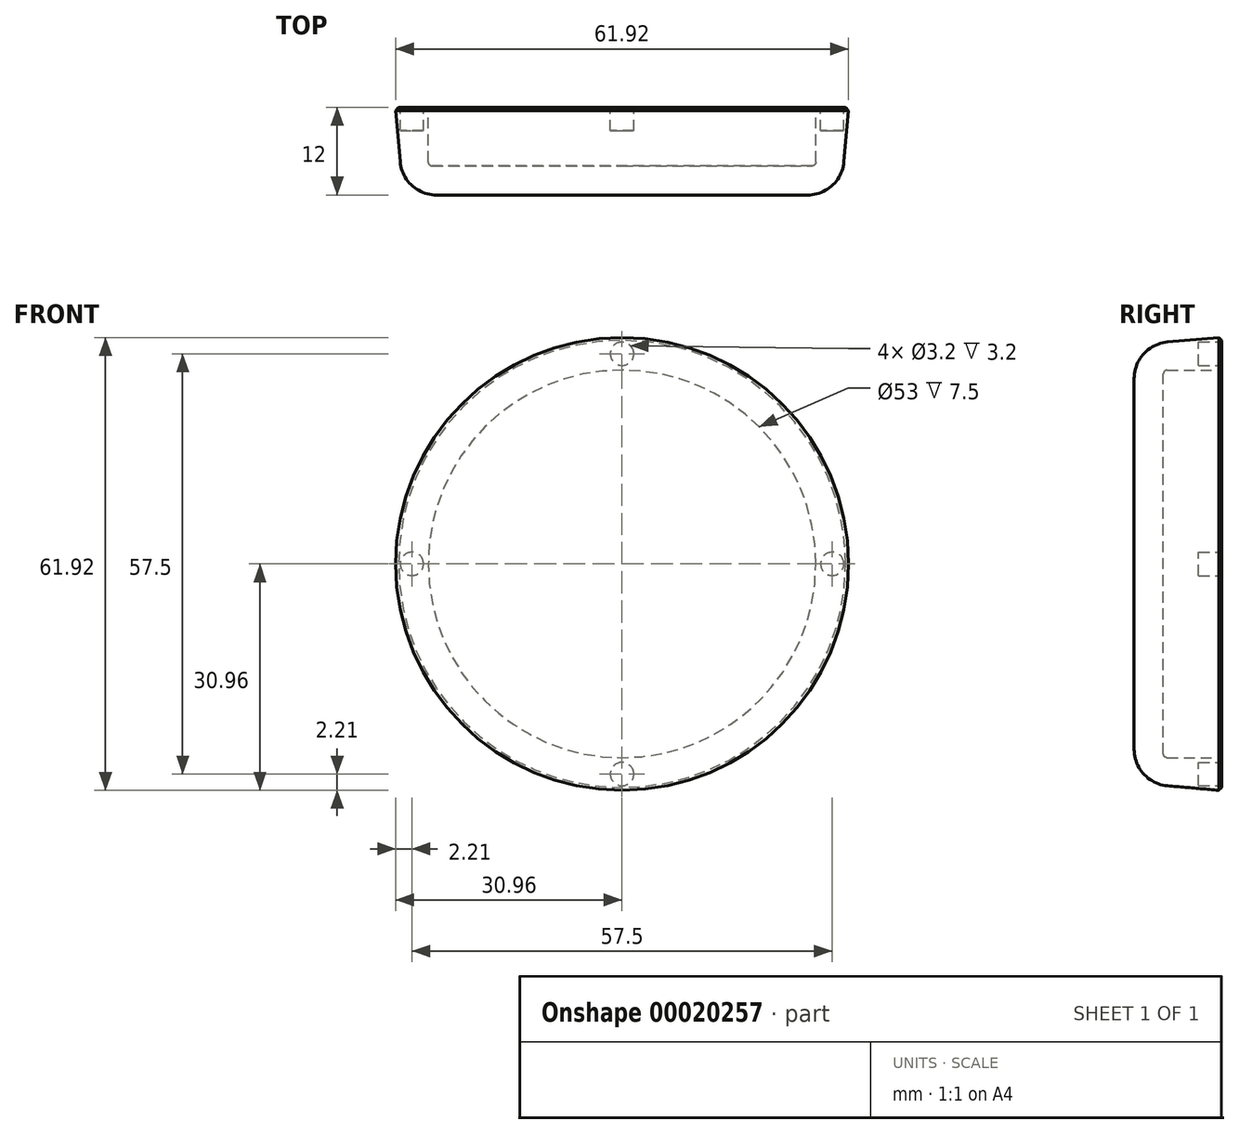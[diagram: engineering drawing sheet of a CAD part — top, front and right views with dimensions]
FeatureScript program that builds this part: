
annotation { "Feature Type Name" : "Feature", "Feature Type Description" : "" }
export const myFeature = defineFeature(function(context is Context, id is Id, definition is map)
    precondition{}
    {
        {
            var Q0;
            Q0=qCreatedBy(makeId("Front.planeOp"),FACE);
            var sketch = newSketch(context, id + "F0", { "sketchPlane" : qUnion([Q0])});
            skCircle(sketch, "E0", {"center": v(0, 0) * mm, "radius": 31 * mm});
            skCircle(sketch, "E1", {"center": v(0, 0) * mm, "radius": 26.5 * mm});
            skSolve(sketch);
        }
        {
            var Q0;
            Q0=makeQuery(id+"F0.imprint","IMPRINT",FACE,{"disambiguationData":[TD([[makeQuery(id+"F0.imprint","IMPRINT",EDGE,{"derivedFrom":sQuery(id+"F0.wireOp",EDGE,"E0")}),1.0]])]});
            var Q1;
            Q1=makeQuery(id+"F0.imprint","IMPRINT",FACE,{"disambiguationData":[TD([[makeQuery(id+"F0.imprint","IMPRINT",EDGE,{"derivedFrom":sQuery(id+"F0.wireOp",EDGE,"E1")}),1.0]])]});
            extrude(context, id + "F1", {"entities" : qUnion([Q0, Q1]), "depth" : 12 * mm, "hasDraft" : true, "draftAngle" : 5 * degree, "draftPullDirection" : true});
        }
        {
            var Q0;
            Q0=makeQuery(id+"F0.imprint","IMPRINT",FACE,{"disambiguationData":[TD([[makeQuery(id+"F0.imprint","IMPRINT",EDGE,{"derivedFrom":sQuery(id+"F0.wireOp",EDGE,"E1")}),1.0]])]});
            var Q1;
            Q1=sQuery(id+"F0.wireOp",EDGE,"E1");
            extrude(context, id + "F2", {"entities" : qUnion([Q0]), "operationType" : NewBodyOperationType.REMOVE, "surfaceEntities" : qUnion([Q1]), "depth" : 8 * mm});
        }
        {
            var Q0;
            Q0=makeQuery(id+"F0.imprint","IMPRINT",FACE,{"disambiguationData":[TD([[makeQuery(id+"F0.imprint","IMPRINT",EDGE,{"derivedFrom":sQuery(id+"F0.wireOp",EDGE,"E0")}),1.0]])]});
            var sketch = newSketch(context, id + "F3", { "sketchPlane" : qUnion([Q0])});
            skCircle(sketch, "E2", {"center": v(0, 0) * mm, "radius": 28.75 * mm, "construction": true});
            skCircle(sketch, "E3", {"center": v(0, 28.75) * mm, "radius": 1.6 * mm});
            skCircle(sketch, "E4.1.0", {"center": v(-28.75, 0) * mm, "radius": 1.6 * mm});
            skCircle(sketch, "E4.2.0", {"center": v(0, -28.75) * mm, "radius": 1.6 * mm});
            skCircle(sketch, "E4.3.0", {"center": v(28.75, 0) * mm, "radius": 1.6 * mm});
            skSolve(sketch);
        }
        {
            var Q0;
            Q0 = qSketchRegion(id + "F3", true);
            extrude(context, id + "F4", {"entities" : qUnion([Q0]), "operationType" : NewBodyOperationType.REMOVE, "depth" : 3.2 * mm});
        }
        {
            var Q0;
            Q0=makeQuery(id+"F1.opExtrude","CAP_EDGE",EDGE,{"disambiguationData":[OSD([sQuery(id+"F0.wireOp",EDGE,"E0")])],"isStart":false});
            fillet(context, id + "F5", {"entities" : qUnion([Q0]), "radius" : 5 * mm, "tangentPropagation" : true, "allowEdgeOverflow" : false});
        }
        {
            var Q0;
            Q0=makeQuery(id+"F2.boolean.opBoolean","COPY",EDGE,{"derivedFrom":makeQuery(id+"F2.opExtrude","CAP_EDGE",EDGE,{"disambiguationData":[OSD([sQuery(id+"F0.wireOp",EDGE,"E1")])],"isStart":false})});
            fillet(context, id + "F6", {"entities" : qUnion([Q0]), "radius" : .5 * mm, "tangentPropagation" : true, "allowEdgeOverflow" : false});
        }
        {
            var Q0;
            Q0=makeQuery(id+"F2.boolean.opBoolean","COPY",EDGE,{"derivedFrom":makeQuery(id+"F2.opExtrude","CAP_EDGE",EDGE,{"disambiguationData":[OSD([sQuery(id+"F0.wireOp",EDGE,"E1")])],"isStart":true})});
            var Q1;
            Q1=makeQuery(id+"F1.opExtrude","CAP_EDGE",EDGE,{"disambiguationData":[OSD([sQuery(id+"F0.wireOp",EDGE,"E0")])],"isStart":true});
            chamfer(context, id + "F7", {"entities" : qUnion([Q0, Q1]), "width" : .4 * mm, "tangentPropagation" : true});
        }
    });
